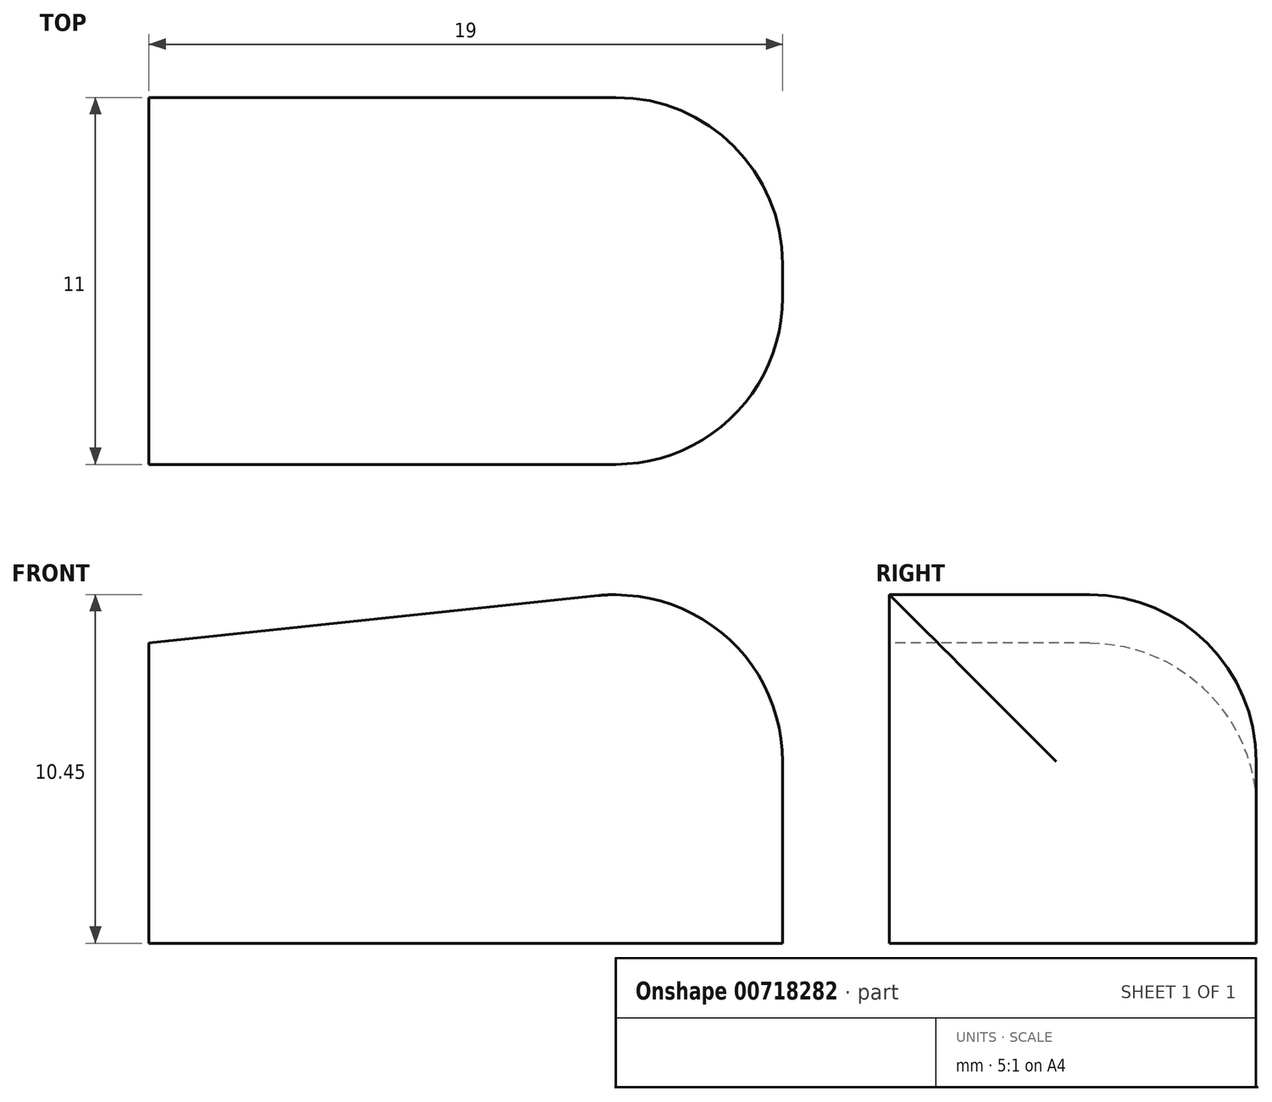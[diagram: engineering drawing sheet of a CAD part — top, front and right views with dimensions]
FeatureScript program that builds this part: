
annotation { "Feature Type Name" : "Feature", "Feature Type Description" : "" }
export const myFeature = defineFeature(function(context is Context, id is Id, definition is map)
    precondition{}
    {
        {
            var Q0;
            Q0=qCreatedBy(makeId("Top.planeOp"),FACE);
            var sketch = newSketch(context, id + "F0", { "sketchPlane" : qUnion([Q0])});
            skLineSegment(sketch, "E0.bottom", {"start": v(9.5, -5.5) * mm, "end": v(-9.5, -5.5) * mm});
            skLineSegment(sketch, "E0.top", {"start": v(9.5, 5.5) * mm, "end": v(-9.5, 5.5) * mm});
            skLineSegment(sketch, "E0.left", {"start": v(9.5, -5.5) * mm, "end": v(9.5, 5.5) * mm});
            skLineSegment(sketch, "E0.right", {"start": v(-9.5, -5.5) * mm, "end": v(-9.5, 5.5) * mm});
            skPoint(sketch, "E0.middle", {"position": v(0, 0) * mm});
            skSolve(sketch);
        }
        {
            var Q0;
            Q0 = qSketchRegion(id + "F0", true);
            extrude(context, id + "F1", {"entities" : qUnion([Q0]), "depth" : 11 * mm, "offsetDistance" : 25 * mm});
        }
        {
            var Q0;
            Q0=makeQuery(id+"F1.opExtrude","SWEPT_FACE",FACE,{"disambiguationData":[OSD([sQuery(id+"F0.wireOp",EDGE,"E0.bottom")])]});
            var sketch = newSketch(context, id + "F2", { "sketchPlane" : qUnion([Q0])});
            skLineSegment(sketch, "E1", {"start": v(-9.5, 9) * mm, "end": v(9.5, 11) * mm});
            skSolve(sketch);
        }
        {
            var Q0;
            {var subQ0=sQuery(id+"F2.wireOp",EDGE,"E1");Q0=makeQuery(id+"F2.imprint","IMPRINT",FACE,{"disambiguationData":[TD([[makeQuery(id+"F2.imprint","IMPRINT",EDGE,{"derivedFrom":subQ0}),1.0]])]});}
            extrude(context, id + "F3", {"entities" : qUnion([Q0]), "operationType" : NewBodyOperationType.REMOVE, "oppositeDirection" : true, "depth" : 25 * mm, "offsetDistance" : 25 * mm});
        }
        {
            var Q0;
            Q0=makeQuery(id+"F3.boolean.opBoolean","COPY",EDGE,{"derivedFrom":makeQuery(id+"F3.opExtrude","CAP_EDGE",EDGE,{"disambiguationData":[OSD([sQuery(id+"F2.wireOp",EDGE,"E1")])],"isStart":true})});
            var Q1;
            {var subQ0=sQuery(id+"F0.wireOp",EDGE,"E0.left");Q1=makeQuery(id+"F3.boolean.opBoolean","MERGE",EDGE,{"derivedFrom":[makeQuery(id+"F1.opExtrude","CAP_EDGE",EDGE,{"disambiguationData":[OSD([subQ0])],"isStart":false}),makeQuery(id+"F3.opExtrude","SWEPT_EDGE",EDGE,{"disambiguationData":[OSD([sQuery(id+"F0.wireOp",EDGE,"E0.bottom"),subQ0,sQuery(id+"F2.wireOp",EDGE,"E1")])]})]});}
            var Q2;
            Q2=makeQuery(id+"F3.boolean.opBoolean","INTERSECT",EDGE,{"derivedFrom":[makeQuery(id+"F1.opExtrude","SWEPT_FACE",FACE,{"disambiguationData":[OSD([sQuery(id+"F0.wireOp",EDGE,"E0.top")])]}),makeQuery(id+"F3.opExtrude","SWEPT_FACE",FACE,{"disambiguationData":[OSD([sQuery(id+"F2.wireOp",EDGE,"E1")])]})]});
            var Q3;
            Q3=makeQuery(id+"F1.opExtrude","SWEPT_EDGE",EDGE,{"disambiguationData":[OSD([sQuery(id+"F0.wireOp",EDGE,"E0.bottom"),sQuery(id+"F0.wireOp",EDGE,"E0.left")])]});
            var Q4;
            Q4=makeQuery(id+"F1.opExtrude","SWEPT_EDGE",EDGE,{"disambiguationData":[OSD([sQuery(id+"F0.wireOp",EDGE,"E0.top"),sQuery(id+"F0.wireOp",EDGE,"E0.left")])]});
            fillet(context, id + "F4", {"entities" : qUnion([Q0, Q1, Q2, Q3, Q4]), "radius" : 5 * mm, "tangentPropagation" : true, "allowEdgeOverflow" : false});
        }
    });
